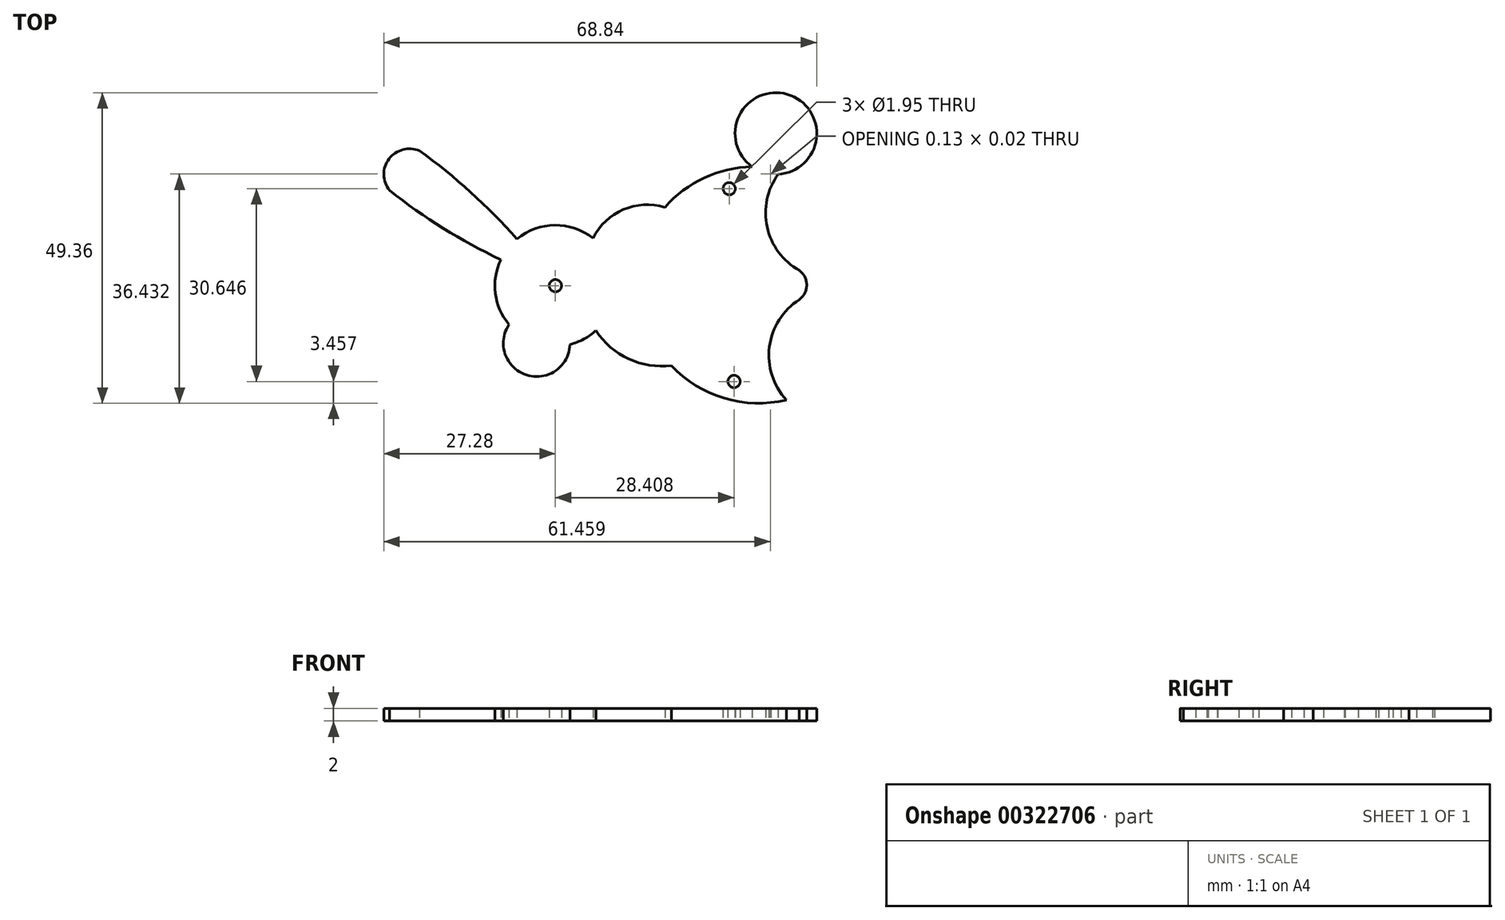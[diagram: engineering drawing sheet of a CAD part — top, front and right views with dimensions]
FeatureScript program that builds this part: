
annotation { "Feature Type Name" : "Feature", "Feature Type Description" : "" }
export const myFeature = defineFeature(function(context is Context, id is Id, definition is map)
    precondition{}
    {
        {
            var Q0;
            Q0=qCreatedBy(makeId("Top.planeOp"),FACE);
            var sketch = newSketch(context, id + "F0", { "sketchPlane" : qUnion([Q0])});
            skSolve(sketch);
        }
        {
            var Q0;
            Q0=qCreatedBy(makeId("Top.planeOp"),FACE);
            var sketch = newSketch(context, id + "F1", { "sketchPlane" : qUnion([Q0])});
            skArc(sketch, "E0", {"start": v(-3.09, 7.53) * mm, "mid": v(-9.15, 9.62) * mm, "end": v(-15.18, 7.43) * mm});
            skArc(sketch, "E1", {"start": v(-16.44, -6.18) * mm, "mid": v(-13.68, -14.19) * mm, "end": v(-6.75, -9.34) * mm});
            skArc(sketch, "E2", {"start": v(-2.62, -7.14) * mm, "mid": v(2.6, -11.64) * mm, "end": v(9.4, -12.7) * mm});
            skArc(sketch, "E3", {"start": v(-35.43, 15.14) * mm, "mid": v(-26.91, 9.13) * mm, "end": v(-17.75, 4.14) * mm});
            skArc(sketch, "E4", {"start": v(-15.18, 7.43) * mm, "mid": v(-22.54, 14.86) * mm, "end": v(-30.67, 21.43) * mm});
            skArc(sketch, "E5", {"start": v(8.35, 12.45) * mm, "mid": v(1.73, 12.1) * mm, "end": v(-3.09, 7.53) * mm});
            skArc(sketch, "E6", {"start": v(22.2, 18.92) * mm, "mid": v(14.6, 17.14) * mm, "end": v(8.35, 12.45) * mm});
            skArc(sketch, "E7", {"start": v(25.05, 17.76) * mm, "mid": v(25.1, 17.75) * mm, "end": v(25.17, 17.74) * mm});
            skPoint(sketch, "E7.second.point", {"position": v(26.36, 17.7) * mm});
            skPoint(sketch, "E7.third.point", {"position": v(28.72, 30.08) * mm});
            skArc(sketch, "E8", {"start": v(9.4, -12.7) * mm, "mid": v(17.8, -17.88) * mm, "end": v(27.65, -18.15) * mm});
            skArc(sketch, "E9", {"start": v(29.72, -2.22) * mm, "mid": v(24.97, -9.7) * mm, "end": v(27.65, -18.15) * mm});
            skArc(sketch, "E10", {"start": v(26.36, 17.7) * mm, "mid": v(24.6, 9.31) * mm, "end": v(29.72, 2.45) * mm});
            skArc(sketch, "E11", {"start": v(29.72, -2.22) * mm, "mid": v(30.89, 0.11) * mm, "end": v(29.72, 2.45) * mm});
            skPoint(sketch, "E12.first.point", {"position": v(17.4, 6.72) * mm});
            skPoint(sketch, "E12.third.point", {"position": v(13.71, 2.37) * mm});
            skArc(sketch, "E13", {"start": v(15.84, 16.59) * mm, "mid": v(19.33, 12.54) * mm, "end": v(20.39, 17.78) * mm});
            skArc(sketch, "E14", {"start": v(21.18, -17.56) * mm, "mid": v(20.06, -12.34) * mm, "end": v(16.61, -16.42) * mm});
            skArc(sketch, "E15", {"start": v(-12, -0.5) * mm, "mid": v(-10.53, -2.59) * mm, "end": v(-7.98, -2.77) * mm});
            skCircle(sketch, "E16", {"center": v(-9.07, 0) * mm, "radius": 0.97 * mm});
            skCircle(sketch, "E17", {"center": v(18.57, 15.42) * mm, "radius": 0.97 * mm});
            skCircle(sketch, "E18", {"center": v(19.34, -15.22) * mm, "radius": 0.97 * mm});
            skArc(sketch, "E19.0", {"start": v(25.17, 17.74) * mm, "mid": v(23.68, 8.81) * mm, "end": v(29.17, 1.6) * mm});
            skCircle(sketch, "E20.0", {"center": v(26, 24.19) * mm, "radius": 5.5 * mm});
            skArc(sketch, "E21.0", {"start": v(29.15, -1.4) * mm, "mid": v(24.11, -8.75) * mm, "end": v(25.85, -17.48) * mm});
            skArc(sketch, "E22.0", {"start": v(29.15, -1.4) * mm, "mid": v(29.89, 0.1) * mm, "end": v(29.17, 1.6) * mm});
            skArc(sketch, "E23.0", {"start": v(9.77, -11.63) * mm, "mid": v(12.91, -14.43) * mm, "end": v(16.61, -16.42) * mm});
            skArc(sketch, "E24.trimOffspring", {"start": v(21.18, -17.56) * mm, "mid": v(23.52, -17.67) * mm, "end": v(25.85, -17.48) * mm});
            skArc(sketch, "E25.0", {"start": v(-2.42, -5.49) * mm, "mid": v(2.67, -10.57) * mm, "end": v(9.77, -11.63) * mm});
            skArc(sketch, "E26.0", {"start": v(8.67, 11.28) * mm, "mid": v(1.79, 11.02) * mm, "end": v(-2.7, 5.8) * mm});
            skArc(sketch, "E27.0", {"start": v(25.17, 17.74) * mm, "mid": v(22.78, 17.92) * mm, "end": v(20.39, 17.78) * mm});
            skArc(sketch, "E28.trimOffspring", {"start": v(15.84, 16.59) * mm, "mid": v(11.92, 14.38) * mm, "end": v(8.67, 11.28) * mm});
            skArc(sketch, "E29.trimOffspring", {"start": v(26.36, 17.7) * mm, "mid": v(27.82, 30.42) * mm, "end": v(22.2, 18.92) * mm});
            skArc(sketch, "E30.0", {"start": v(-2.7, 5.8) * mm, "mid": v(-3.54, 6.62) * mm, "end": v(-4.49, 7.3) * mm});
            skArc(sketch, "E31.trimOffspring", {"start": v(-6.75, -9.34) * mm, "mid": v(-4.55, -8.5) * mm, "end": v(-2.62, -7.14) * mm});
            skArc(sketch, "E32.trimOffspring", {"start": v(-6.81, -8.32) * mm, "mid": v(-6, -8.05) * mm, "end": v(-5.2, -7.7) * mm});
            skArc(sketch, "E33.trimOffspring", {"start": v(-17.75, 4.14) * mm, "mid": v(-18.61, -1.22) * mm, "end": v(-16.44, -6.18) * mm});
            skArc(sketch, "E34.0", {"start": v(-15.13, -6.15) * mm, "mid": v(-13.38, -13.24) * mm, "end": v(-7.79, -8.53) * mm});
            skArc(sketch, "E35", {"start": v(-15.8, -5.4) * mm, "mid": v(-15.47, -5.78) * mm, "end": v(-15.13, -6.15) * mm});
            skArc(sketch, "E36.trimOffspring", {"start": v(-7.79, -8.53) * mm, "mid": v(-7.3, -8.44) * mm, "end": v(-6.81, -8.32) * mm});
            skArc(sketch, "E37.0", {"start": v(-34.94, 16.03) * mm, "mid": v(-26, 9.74) * mm, "end": v(-16.36, 4.6) * mm});
            skArc(sketch, "E38.0", {"start": v(-15.26, 6) * mm, "mid": v(-22.8, 13.74) * mm, "end": v(-31.18, 20.56) * mm});
            skArc(sketch, "E39", {"start": v(-30.67, 21.43) * mm, "mid": v(-35.53, 20.16) * mm, "end": v(-35.43, 15.14) * mm});
            skArc(sketch, "E40", {"start": v(-31.18, 20.56) * mm, "mid": v(-34.74, 19.7) * mm, "end": v(-34.94, 16.03) * mm});
            skArc(sketch, "E41.trimOffspring", {"start": v(-16.36, 4.6) * mm, "mid": v(-17.26, 2.67) * mm, "end": v(-17.67, 0.6) * mm});
            skLineSegment(sketch, "E42", {"start": v(-7.23, 2.34) * mm, "end": v(-4.49, 7.3) * mm});
            skLineSegment(sketch, "E43", {"start": v(-5.37, 7.79) * mm, "end": v(-8.12, 2.82) * mm});
            skLineSegment(sketch, "E44", {"start": v(-11.98, 0.6) * mm, "end": v(-17.67, 0.6) * mm});
            skLineSegment(sketch, "E45", {"start": v(-17.68, -0.5) * mm, "end": v(-12, -0.5) * mm});
            skLineSegment(sketch, "E46", {"start": v(-5.2, -7.7) * mm, "end": v(-7.98, -2.77) * mm});
            skLineSegment(sketch, "E47", {"start": v(-4.4, -7.24) * mm, "end": v(-7.18, -2.3) * mm});
            skArc(sketch, "E48.trimOffspring", {"start": v(-17.68, -0.5) * mm, "mid": v(-17.12, -3.1) * mm, "end": v(-15.8, -5.4) * mm});
            skArc(sketch, "E49.trimOffspring", {"start": v(-8.12, 2.82) * mm, "mid": v(-10.55, 2.58) * mm, "end": v(-11.98, 0.6) * mm});
            skArc(sketch, "E50.trimOffspring", {"start": v(-7.18, -2.3) * mm, "mid": v(-6.1, 0.03) * mm, "end": v(-7.23, 2.34) * mm});
            skArc(sketch, "E51.trimOffspring", {"start": v(-4.4, -7.24) * mm, "mid": v(-3.34, -6.44) * mm, "end": v(-2.42, -5.49) * mm});
            skArc(sketch, "E52.trimOffspring", {"start": v(-5.37, 7.79) * mm, "mid": v(-10.6, 8.48) * mm, "end": v(-15.26, 6) * mm});
            skSolve(sketch);
        }
        {
            var Q0;
            Q0=makeQuery(id+"F1.imprint","IMPRINT",FACE,{"disambiguationData":[TD([[makeQuery(id+"F1.imprint","IMPRINT",EDGE,{"derivedFrom":sQuery(id+"F1.wireOp",EDGE,"E0")}),1.0]])]});
            var Q1;
            {var subQ1=sQuery(id+"F1.wireOp",EDGE,"E7");Q1=makeQuery(id+"F1.imprint","IMPRINT",FACE,{"disambiguationData":[TD([[makeQuery(id+"F1.imprint","IMPRINT",EDGE,{"derivedFrom":subQ1}),-1.0]])]});}
            var Q2;
            Q2=makeQuery(id+"F1.imprint","IMPRINT",FACE,{"disambiguationData":[TD([[makeQuery(id+"F1.imprint","IMPRINT",EDGE,{"derivedFrom":sQuery(id+"F1.wireOp",EDGE,"E37.0")}),1.0]])]});
            var Q3;
            Q3=makeQuery(id+"F1.imprint","IMPRINT",FACE,{"disambiguationData":[TD([[makeQuery(id+"F1.imprint","IMPRINT",EDGE,{"derivedFrom":sQuery(id+"F1.wireOp",EDGE,"E15")}),-1.0]])]});
            var Q4;
            Q4=makeQuery(id+"F1.imprint","IMPRINT",FACE,{"disambiguationData":[TD([[makeQuery(id+"F1.imprint","IMPRINT",EDGE,{"derivedFrom":sQuery(id+"F1.wireOp",EDGE,"E20.0")}),1.0]])]});
            extrude(context, id + "F2", {"entities" : qUnion([Q0, Q1, Q2, Q3, Q4]), "depth" : 2 * mm});
        }
        {
            var Q0;
            Q0=sQuery(id+"F1.wireOp",EDGE,"E17");
            extrude(context, id + "F3", {"bodyType" : ToolBodyType.SURFACE, "surfaceEntities" : qUnion([Q0]), "depth" : 4 * mm});
        }
        {
            var Q0;
            Q0=sQuery(id+"F1.wireOp",EDGE,"E16");
            extrude(context, id + "F4", {"bodyType" : ToolBodyType.SURFACE, "surfaceEntities" : qUnion([Q0]), "depth" : 4 * mm});
        }
        {
            var Q0;
            Q0=sQuery(id+"F1.wireOp",EDGE,"E18");
            extrude(context, id + "F5", {"bodyType" : ToolBodyType.SURFACE, "surfaceEntities" : qUnion([Q0]), "depth" : 4 * mm});
        }
    });
